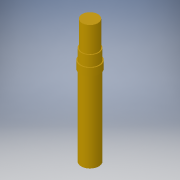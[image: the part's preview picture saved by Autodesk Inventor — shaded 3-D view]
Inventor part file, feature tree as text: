
AUTODESK INVENTOR PART (.ipt)
format: ipt  version: 2019 (Build 230136000, 136)  size: 130,560 bytes
history: native  units: in
note: dims shown in document units (in); Inventor stores cm internally (conversion verified against a paired STEP export)
features: extrude x5, sketch x5, projected_geometry x4
ambient origin geometry x8: Origin, YZ Plane, XZ Plane, XY Plane, X Axis, Y Axis, Z Axis, Center Point
bodies: Solid1 (feature_tree)
feature tree (14):
  extrude  "Extrusion1"  Depth=0.3435in TaperAngle=0.0deg
  extrude  "Extrusion2"  Depth=0.0315in TaperAngle=0.0deg
  extrude  "Extrusion3"  Depth=0.045in TaperAngle=0.0deg
  extrude  "Extrusion4"  Depth=0.1075in TaperAngle=0.0deg
  extrude  "Extrusion5"  Depth=0.3in TaperAngle=0.0deg
  sketch  "Sketch1"  dims[d0=0.075in d1=0.3435in d2=0.0in]
  sketch  "Sketch2"  dims[d3=0.0835in d4=0.0315in d5=0.0in]
  projected_geometry  "Projected Loop1"
  sketch  "Sketch3"  dims[d6=0.0695in d7=0.045in d8=0.0in]
  projected_geometry  "Projected Loop2"
  sketch  "Sketch4"  dims[d9=0.0675in d10=0.1075in d11=0.0in]
  projected_geometry  "Projected Loop3"
  sketch  "Sketch5"  dims[d12=0.045in d13=0.3in d14=0.0in]
  projected_geometry  "Projected Loop4"
